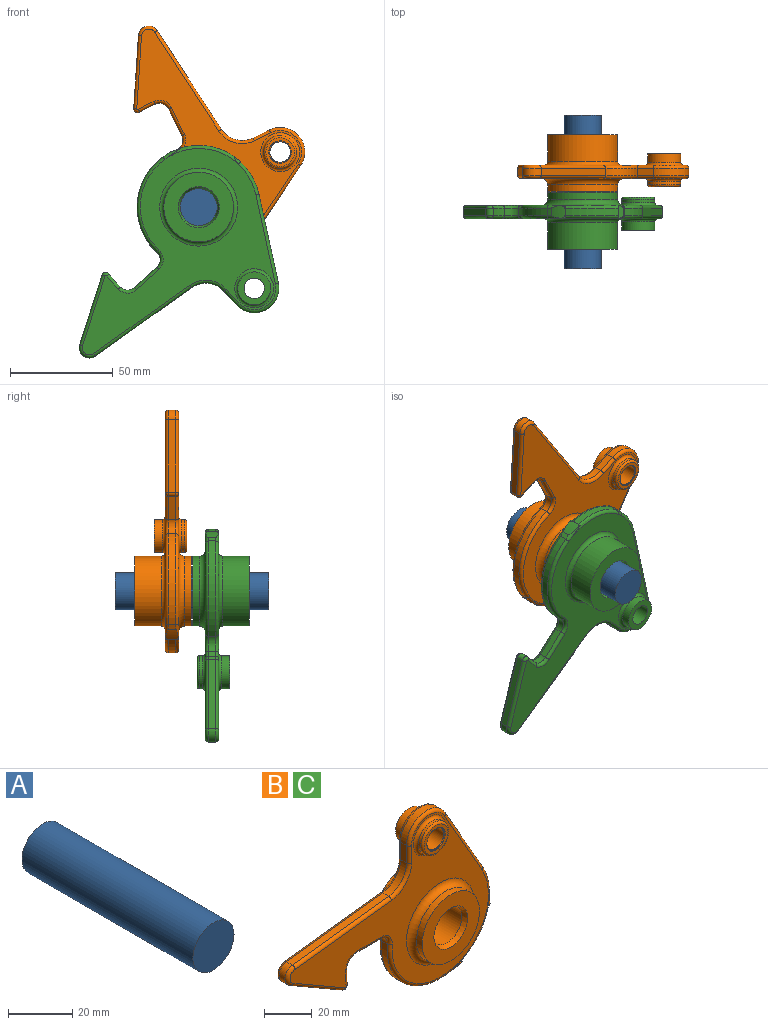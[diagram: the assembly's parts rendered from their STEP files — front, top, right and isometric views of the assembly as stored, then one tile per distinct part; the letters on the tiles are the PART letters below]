
ASSEMBLY  parts=3 mates=2
PART A: 3 faces, bbox 18x75x18 mm
  f0: cylinder r=9mm len=75mm, axis (0,1,0), area 4241.2mm2, adj f1,f2
  f1: plane 18x18mm, normal (0,-1,0), area 254.5mm2, adj f0
  f2: plane 18x18mm, normal (0,1,0), area 254.5mm2, adj f0
PART B: 77 faces, bbox 123.4x27.8x93 mm
  f0: plane 117.5x86.5mm, normal (0,1,0), area 3019.4mm2, adj f4,f5,f42,f43,f44,f45,f46,f47
  f1: torus R=9.5mm, axis (0,-1,0), area 126.5mm2, adj f2,f20
  f2: cylinder r=8mm len=16mm, axis (0,1,0), area 75.4mm2, adj f1,f62
  f3: plane 14x14mm, normal (0,-1,0), area 58.9mm2, adj f62,f67
  f4: torus R=9.5mm, axis (0,-1,0), area 126.5mm2, adj f0,f60
  f5: torus R=19mm, axis (0,-1,0), area 349.9mm2, adj f0,f58
  f6: torus R=20mm, axis (0,-1,0), area 535.6mm2, adj f7,f20
  f7: cylinder r=17mm len=34mm, axis (0,1,0), area 347.1mm2, adj f6,f8
  f8: plane 34x34mm, normal (0,-1,0), area 593.8mm2, adj f7,f64
  f9: cylinder r=56mm len=8.43mm, axis (0,1,0), area 29.5mm2, adj f23,f25,f36,f52
  f10: plane 30.75x17.75mm, normal (-0.5,0,-0.87), area 124.3mm2, adj f11,f25,f33,f49
  f11: cylinder r=5mm len=9.3mm, axis (0,1,0), area 43.7mm2, adj f10,f12,f31,f47
  f12: plane 57.01x6.79mm, normal (-0.12,0,0.99), area 200.9mm2, adj f11,f21,f29,f45
  f13: plane 8.83x3.5mm, normal (-1,0,0), area 30.9mm2, adj f14,f21,f26,f42
  f14: cylinder r=12mm len=22.41mm, axis (0,1,0), area 110.1mm2, adj f13,f15,f28,f44
  f15: plane 38.54x22.11mm, normal (0.87,0,0.5), area 155.5mm2, adj f14,f16,f30,f46
  f16: cylinder r=30mm len=17.5mm, axis (0,1,0), area 63.7mm2, adj f15,f24,f32,f48
  f17: plane 3.5x2.55mm, normal (0.12,0,-0.99), area 9mm2, adj f18,f41,f57,f74
  f18: cylinder r=30mm len=33.55mm, axis (0,1,0), area 186.4mm2, adj f17,f22,f40,f56
  f19: plane 14.58x3.5mm, normal (0,0,-1), area 51mm2, adj f22,f23,f38,f54
  f20: plane 117.5x86.5mm, normal (0,-1,0), area 2896.8mm2, adj f1,f6,f26,f27,f28,f29,f30,f31
  f21: cylinder r=12mm len=11.92mm, axis (0,-1,0), area 61mm2, adj f12,f13,f27,f43
  f22: cylinder r=5mm len=5.43mm, axis (0,1,0), area 29mm2, adj f18,f19,f39,f55
  f23: cylinder r=5mm len=4.99mm, axis (0,1,0), area 26.5mm2, adj f9,f19,f37,f53
  f24: cylinder r=5mm len=3.5mm, axis (0,1,0), area 3.4mm2, adj f16,f34,f50,f73
  f25: cylinder r=2mm len=3.5mm, axis (0,1,0), area 15.3mm2, adj f9,f10,f35,f51
  f26: cylinder r=1.5mm len=8.83mm, axis (0,0,1), area 20.8mm2, adj f13,f20,f27,f28
  f27: torus R=13.5mm, axis (0,-1,0), area 42.9mm2, adj f20,f21,f26,f29
  f28: torus R=10.5mm, axis (0,-1,0), area 70.7mm2, adj f14,f20,f26,f30
  f29: cylinder r=1.5mm len=57.19mm, axis (0.99,0,0.12), area 135.3mm2, adj f12,f20,f27,f31
  f30: cylinder r=1.5mm len=39.29mm, axis (0.5,0,-0.87), area 104.7mm2, adj f15,f20,f28,f32
  f31: torus R=3.5mm, axis (0,-1,0), area 26.2mm2, adj f11,f20,f29,f33
  f32: torus R=28.5mm, axis (0,-1,0), area 42.1mm2, adj f16,f20,f30,f34
  f33: cylinder r=1.5mm len=31.5mm, axis (-0.87,0,0.5), area 83.7mm2, adj f10,f20,f31,f35
  f34: torus R=6.5mm, axis (0,-1,0), area 5.6mm2, adj f20,f24,f32,f72,f73
  f35: torus R=0.5mm, axis (0,-1,0), area 7.5mm2, adj f20,f25,f33,f36
  f36: torus R=57.5mm, axis (0,-1,0), area 20.1mm2, adj f9,f20,f35,f37
  f37: torus R=6.5mm, axis (0,-1,0), area 19.8mm2, adj f20,f23,f36,f38
  f38: cylinder r=1.5mm len=14.58mm, axis (-1,0,0), area 34.3mm2, adj f19,f20,f37,f39
  f39: torus R=6.5mm, axis (0,-1,0), area 21.6mm2, adj f20,f22,f38,f40
  f40: torus R=28.5mm, axis (0,-1,0), area 123.2mm2, adj f18,f20,f39,f41
  f41: cylinder r=1.5mm len=9.82mm, axis (-0.99,0,-0.12), area 13.7mm2, adj f17,f20,f40,f71,f74
  f42: cylinder r=1.5mm len=8.83mm, axis (0,0,-1), area 20.8mm2, adj f0,f13,f43,f44
  f43: torus R=13.5mm, axis (0,-1,0), area 42.9mm2, adj f0,f21,f42,f45
  f44: torus R=10.5mm, axis (0,-1,0), area 70.7mm2, adj f0,f14,f42,f46
  f45: cylinder r=1.5mm len=57.19mm, axis (-0.99,0,-0.12), area 135.3mm2, adj f0,f12,f43,f47
  f46: cylinder r=1.5mm len=39.29mm, axis (-0.5,0,0.87), area 104.7mm2, adj f0,f15,f44,f48
  f47: torus R=3.5mm, axis (0,-1,0), area 26.2mm2, adj f0,f11,f45,f49
  f48: torus R=28.5mm, axis (0,-1,0), area 42.1mm2, adj f0,f16,f46,f50
  f49: cylinder r=1.5mm len=31.5mm, axis (0.87,0,-0.5), area 83.7mm2, adj f0,f10,f47,f51
  f50: torus R=6.5mm, axis (0,-1,0), area 5.6mm2, adj f0,f24,f48,f72,f73
  f51: torus R=0.5mm, axis (0,-1,0), area 7.5mm2, adj f0,f25,f49,f52
  f52: torus R=57.5mm, axis (0,-1,0), area 20.1mm2, adj f0,f9,f51,f53
  f53: torus R=6.5mm, axis (0,-1,0), area 19.8mm2, adj f0,f23,f52,f54
  f54: cylinder r=1.5mm len=14.58mm, axis (1,0,0), area 34.3mm2, adj f0,f19,f53,f55
  f55: torus R=6.5mm, axis (0,-1,0), area 21.6mm2, adj f0,f22,f54,f56
  f56: torus R=28.5mm, axis (0,-1,0), area 123.2mm2, adj f0,f18,f55,f57
  f57: cylinder r=1.5mm len=9.82mm, axis (0.99,0,0.12), area 13.7mm2, adj f0,f17,f56,f71,f74
  f58: cylinder r=17mm len=34mm, axis (0,-1,0), area 1388.6mm2, adj f5,f59
  f59: plane 34x34mm, normal (0,1,0), area 593.8mm2, adj f58,f68
  f60: cylinder r=8mm len=16mm, axis (0,1,0), area 201.1mm2, adj f4,f61
  f61: plane 16x16mm, normal (0,1,0), area 122.5mm2, adj f60,f65
  f62: torus R=7mm, axis (0,-1,0), area 75.4mm2, adj f2,f3
  f63: cylinder r=9mm len=22.92mm, axis (0,1,0), area 1296.2mm2, adj f64,f68
  f64: cone r=10mm half-angle=22.5deg, axis (0,-1,0), area 156mm2, adj f8,f63
  f65: cylinder r=5mm len=15.5mm, axis (0,1,0), area 486.9mm2, adj f61,f66
  f66: plane 10.5x10.5mm, normal (0,-1,0), area 8.1mm2, adj f65,f69
  f67: cylinder r=5.5mm len=11mm, axis (0,1,0), area 8.6mm2, adj f3,f69
  f68: cone r=10mm half-angle=22.5deg, axis (0,1,0), area 156mm2, adj f59,f63
  f69: torus R=5.25mm, axis (0,1,0), area 13.3mm2, adj f66,f67
  f70: cylinder r=30.1mm len=20.66mm, axis (0,-1,0), area 95.5mm2, adj f71,f72,f75,f76
  f71: plane 7.28x6.5mm, normal (-0.12,0,0.99), area 3.6mm2, adj f41,f57,f70,f74,f75,f76
  f72: cylinder r=6.5mm len=6.5mm, axis (0,-1,0), area 1.6mm2, adj f34,f50,f70,f73,f75,f76
  f73: cylinder r=30.11mm len=6.5mm, axis (0,-1,0), area 17mm2, adj f24,f34,f50,f72
  f74: cylinder r=30.11mm len=6.92mm, axis (0,-1,0), area 41mm2, adj f17,f41,f57,f71
  f75: torus R=28.6mm, axis (0,-1,0), area 69.7mm2, adj f0,f70,f71,f72
  f76: torus R=28.6mm, axis (0,-1,0), area 69.7mm2, adj f20,f70,f71,f72
PART C: same geometry as B
PLACE A t=(-2.18,29.65,-9.88)mm fixed
PLACE B rot(axis=(0,1,0),63.7deg) t=(-2.18,5.15,-9.88)mm
PLACE C rot(axis=(0.93,0,0.36),180deg) t=(-2.18,-20.85,-9.88)mm
MATE revolute A.f0 <-> C.f5  axis (0,-1,0) through (-2.18,-45.35,-9.88)mm
MATE revolute A.f0 <-> B.f5  axis (0,1,0) through (-2.18,29.65,-9.88)mm
